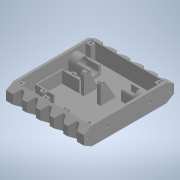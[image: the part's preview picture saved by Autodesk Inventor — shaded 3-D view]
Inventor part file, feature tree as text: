
AUTODESK INVENTOR PART (.ipt)
format: ipt  version: 2020 (Build 240168000, 168)  size: 550,912 bytes
history: native  units: in
note: dims shown in document units (in); Inventor stores cm internally (conversion verified against a paired STEP export)
features: extrude x15, sketch x15, projected_geometry x15, mirror x5, plane x2
ambient origin geometry x8: Origin, YZ Plane, XZ Plane, XY Plane, X Axis, Y Axis, Z Axis, Center Point
bodies: Solid1 (feature_tree)
feature tree (52):
  extrude  "Extrusion1"  Depth=5.9055in
  extrude  "Extrusion2"  TaperAngle=0.0deg  [1 undecoded]
  extrude  "Extrusion3"  Depth=1.063in
  extrude  "Extrusion4"  Depth=0.315in
  extrude  "Extrusion5"  TaperAngle=0.0deg  [1 undecoded]
  extrude  "Extrusion6"  Depth=0.5906in
  mirror  "Mirror1"
  extrude  "Extrusion7"  Depth=0.0787in
  mirror  "Mirror2"
  extrude  "Extrusion8"  Depth=0.6102in
  mirror  "Mirror3"
  plane  "Work Plane1"
  extrude  "Extrusion9"  Depth=0.7874in TaperAngle=0.0deg
  mirror  "Mirror4"
  extrude  "Extrusion10"  Depth=6.063in TaperAngle=0.0deg
  extrude  "Extrusion11"  Depth=0.1575in
  extrude  "Extrusion12"  TaperAngle=0.0deg  [1 undecoded]
  extrude  "Extrusion13"  Depth=0.2756in
  extrude  "Extrusion14"  Depth=0.4331in
  plane  "Work Plane2"
  extrude  "Extrusion16"  Depth=2.7559in
  mirror  "Mirror5"
  sketch  "Sketch1"  dims[d0=1.1811in d1=5.9055in]
  sketch  "Sketch2"  dims[d2=5.1181in d3=0.0in]
  projected_geometry  "Projected Loop1"
  sketch  "Sketch3"  dims[d4=0.1575in d5=1.063in]
  projected_geometry  "Projected Loop2"
  projected_geometry  "Projected Loop3"
  sketch  "Sketch4"  dims[d6=0.0in d8=0.315in]
  sketch  "Sketch5"  dims[d10=0.993in d11=0.0in]
  projected_geometry  "Projected Loop4"
  sketch  "Sketch6"  dims[d12=0.6496in d13=0.5906in]
  sketch  "Sketch7"  dims[d14=1.5748in d15=0.0787in]
  sketch  "Sketch9"  dims[d16=0.5512in d17=0.0in d18=0.6102in]
  sketch  "Sketch10"  dims[d19=0.4803in d20=0.7874in d21=0.0in]
  sketch  "Sketch12"  dims[d22=0.1654in d23=6.063in d24=0.0in]
  projected_geometry  "Projected Loop6"
  projected_geometry  "Projected Loop7"
  projected_geometry  "Projected Loop8"
  sketch  "Sketch13"  dims[d25=0.5114in d26=0.1575in]
  projected_geometry  "Projected Loop9"
  projected_geometry  "Projected Loop10"
  projected_geometry  "Projected Loop11"
  projected_geometry  "Projected Loop12"
  projected_geometry  "Projected Loop13"
  projected_geometry  "Projected Loop14"
  sketch  "Sketch14"  dims[d27=1.5748in d28=0.0in d29=0.0in]
  sketch  "Sketch15"  dims[d30=0.1575in d31=0.2756in]
  projected_geometry  "Projected Loop15"
  sketch  "Sketch16"  dims[d32=0.0in d33=0.4331in]
  sketch  "Sketch18"  dims[d34=0.122in d38=2.7559in d40=0.061in d41=0.0909in d42=0.2362in d43=0.0in d44=60.0deg d45=0.0787in d46=0.315in d48=0.993in d49=0.0in d51=0.1575in d52=0.1575in d53=0.2756in d54=0.0in d55=0.4724in d56=1.2008in d57=1.6142in d58=1.5945in d59=0.0787in d60=0.0787in d62=0.315in d63=0.7677in d64=0.0in d65=0.1575in d66=0.1575in d67=0.2756in d68=0.0in d69=0.8268in d70=0.2953in d71=0.0394in d72=0.0in d76=0.1575in d77=120.0deg d79=0.1969in d80=0.1969in d81=0.1969in d82=0.1969in d83=0.1969in d85=120.0deg d87=1.0902in d88=0.0in]
  projected_geometry  "Projected Loop18"
note: 3 required parameter values undecoded (feature->parameter linkage not recoverable at this tier; creation-order binding heuristic only, values carry confidence <= 0.55)
